# Revit family: SpecEquip_BoilingUnit_Zip UK_On-Wall_HydroBoil
name_source: partatom
category: Specialty Equipment
revit_build: Autodesk Revit 2016 (Build: 20190508_0715(x64)
units: mm (PartAtom-declared; Revit-internal decimal feet)

## family parameters
Always vertical = Yes
Cut with Voids When Loaded = Yes
OmniClass Number = 23.75.70.17.21
OmniClass Title = Embedded Water Heating Terminals
Part Type = Normal
Room Calculation Point = No
Round Connector Dimension = Use Diameter
Shared = No
Work Plane-Based = No

## types (8) — shared parameters
Body Material = z_Zip_White
Description = HydroBoil - On wall boiling water
IfcExportAs = IfcBoiler
IfcExportType = WATER
Manufacturer = ZIP Water UK
Manufacturer_URL__Product Specific = https://specify.zipwater.co.uk
ModifiedIssue_ANZRS = 20190830 $
Tap Material = z_Zip_Stainless Steel
URL = https://www.zipwater.co.uk
Uniclass2015Code = Pr_60_60_96_28
Uniclass2015Title = Electric storage water heaters
Uniclass2015Version = Products v1.14

## per-type parameters (varying)
| type | Manufacturer_Overall Depth | Manufacturer_Overall Height | Manufacturer_Overall Width | Manufacturer_Spec Code | Model | Tap distance | Type Comments |
| 5.0l | 198 mm | 465 mm | 318 mm | 305552 | 305552 | 91 mm | 5.0 Litre Hydroboil |
| 3.0l | 180 mm | 431 mm | 289 mm | 303552 | 303552 | 77 mm | 3.0 Litre Hydroboil |
| 1.5l | 180 mm | 356 mm | 289 mm | 301552 | 301552 | 91 mm | 1.5 Litre Hydroboil |
| 7.0l | 198 mm | 578 mm | 318 mm | 307552 | 307552 | 91 mm | 7.0 Litre Hydroboil |
| 10.0l | 244 mm | 600 mm | 390 mm | 310552 | 310552 | 91 mm | 10.0 Litre Hydroboil |
| 15.0l | 299 mm | 600 mm | 390 mm | 315552 | 315552 | 91 mm | 15.0 Litre Hydroboil |
| 25.0l | 299 mm | 780 mm | 390 mm | 325552 | 325552 | 91 mm | 25.0 Litre Hydroboil |
| 40.0l | 284 mm | 840 mm | 515 mm | 340552 | 340552 | 62 mm | 40.0 Litre Hydroboil |

## geometry (parser evidence)
native form markers: Sweep x3
no freeform markers — native parametric forms only
